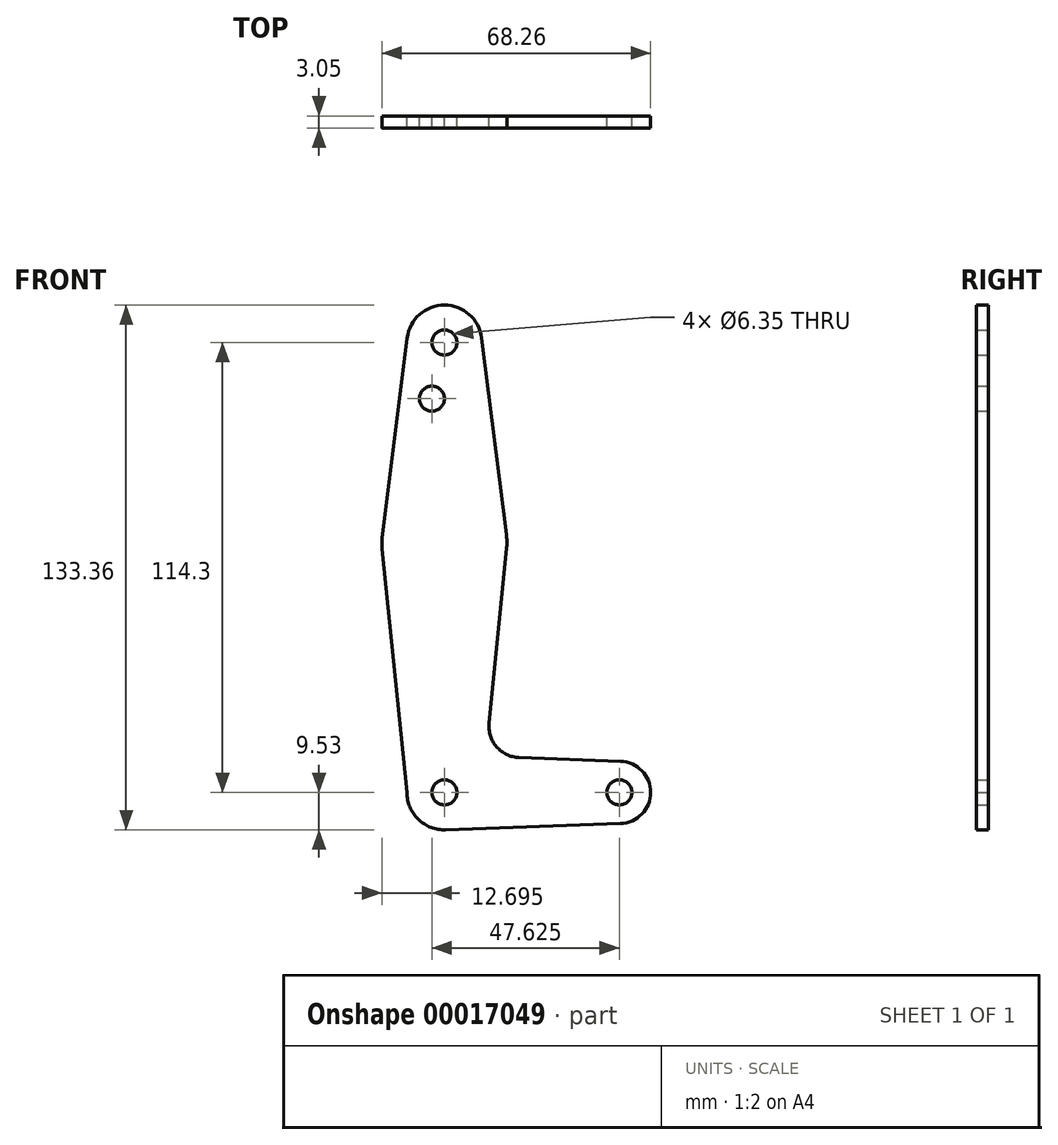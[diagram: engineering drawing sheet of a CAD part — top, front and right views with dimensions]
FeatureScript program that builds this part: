
annotation { "Feature Type Name" : "Feature", "Feature Type Description" : "" }
export const myFeature = defineFeature(function(context is Context, id is Id, definition is map)
    precondition{}
    {
        {
            var Q0;
            Q0=qCreatedBy(makeId("Front.planeOp"),FACE);
            var sketch = newSketch(context, id + "F0", { "sketchPlane" : qUnion([Q0])});
            skLineSegment(sketch, "E0", {"start": v(0, 114.3) * mm, "end": v(0, 0) * mm, "construction": true});
            skLineSegment(sketch, "E1", {"start": v(0, 0) * mm, "end": v(44.45, 0) * mm, "construction": true});
            skCircle(sketch, "E2", {"center": v(0, 114.3) * mm, "radius": 9.53 * mm});
            skCircle(sketch, "E3", {"center": v(0, 63.5) * mm, "radius": 15.88 * mm});
            skCircle(sketch, "E4", {"center": v(0, 0) * mm, "radius": 9.53 * mm});
            skCircle(sketch, "E5", {"center": v(44.45, 0) * mm, "radius": 7.94 * mm});
            skLineSegment(sketch, "E6", {"start": v(-9.45, 115.5) * mm, "end": v(-15.75, 65.48) * mm});
            skLineSegment(sketch, "E7", {"start": v(9.45, 115.5) * mm, "end": v(15.75, 65.48) * mm});
            skLineSegment(sketch, "E8", {"start": v(18.97, 8.85) * mm, "end": v(44.73, 7.93) * mm});
            skLineSegment(sketch, "E9", {"start": v(44.73, -7.93) * mm, "end": v(0.34, -9.52) * mm});
            skLineSegment(sketch, "E10", {"start": v(-9.52, 0) * mm, "end": v(-15.8, 61.9) * mm});
            skLineSegment(sketch, "E11", {"start": v(15.8, 61.91) * mm, "end": v(11.34, 17.6) * mm});
            skCircle(sketch, "E12", {"center": v(0, 114.3) * mm, "radius": 3.18 * mm});
            skCircle(sketch, "E13", {"center": v(-3.17, 100.03) * mm, "radius": 3.18 * mm});
            skCircle(sketch, "E14", {"center": v(0, 0) * mm, "radius": 3.18 * mm});
            skCircle(sketch, "E15", {"center": v(44.45, 0) * mm, "radius": 3.18 * mm});
            skArc(sketch, "E16.filletArc", {"start": v(11.34, 17.6) * mm, "mid": v(13.26, 11.57) * mm, "end": v(18.97, 8.85) * mm});
            skSolve(sketch);
        }
        {
            var Q0;
            Q0 = qSketchRegion(id + "F0", true);
            extrude(context, id + "F1", {"entities" : qUnion([Q0]), "depth" : 3.05 * mm});
        }
    });
